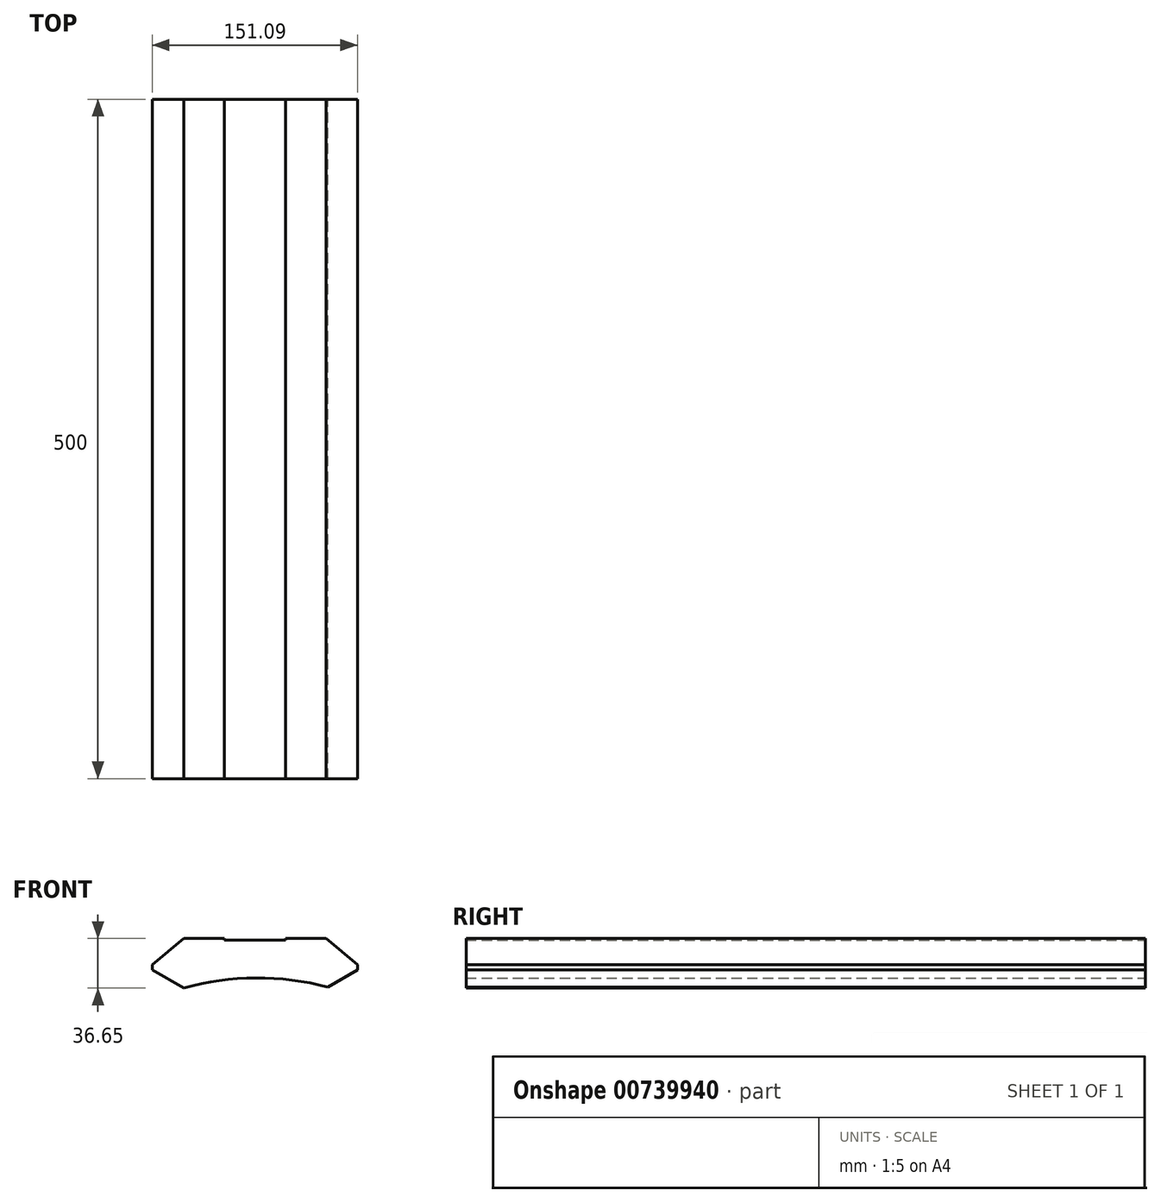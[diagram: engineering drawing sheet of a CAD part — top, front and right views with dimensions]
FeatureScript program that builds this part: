
annotation { "Feature Type Name" : "Feature", "Feature Type Description" : "" }
export const myFeature = defineFeature(function(context is Context, id is Id, definition is map)
    precondition{}
    {
        {
            var Q0;
            Q0=qCreatedBy(makeId("Front.planeOp"),FACE);
            var sketch = newSketch(context, id + "F0", { "sketchPlane" : qUnion([Q0])});
            skLineSegment(sketch, "E0", {"start": v(-68.02, 4) * mm, "end": v(-44.97, 23.34) * mm});
            skLineSegment(sketch, "E1", {"start": v(-44.97, 23.34) * mm, "end": v(-14.97, 23.34) * mm});
            skLineSegment(sketch, "E2", {"start": v(-14.97, 23.34) * mm, "end": v(-14.97, 22.04) * mm});
            skLineSegment(sketch, "E3", {"start": v(-14.97, 22.04) * mm, "end": v(30.03, 22.04) * mm});
            skLineSegment(sketch, "E4", {"start": v(30.03, 22.04) * mm, "end": v(30.03, 23.34) * mm});
            skLineSegment(sketch, "E5", {"start": v(30.03, 23.34) * mm, "end": v(60.03, 23.34) * mm});
            skLineSegment(sketch, "E6", {"start": v(60.03, 23.34) * mm, "end": v(83.07, 4) * mm});
            skLineSegment(sketch, "E7", {"start": v(83.07, 4) * mm, "end": v(83.07, 0) * mm});
            skLineSegment(sketch, "E8", {"start": v(83.07, 0) * mm, "end": v(61.27, -12.6) * mm});
            skLineSegment(sketch, "E9", {"start": v(-68.02, 4) * mm, "end": v(-68.02, 0) * mm});
            skLineSegment(sketch, "E10", {"start": v(-68.02, 0) * mm, "end": v(-44.97, -13.3) * mm});
            skArc(sketch, "E11", {"start": v(61.27, -12.6) * mm, "mid": v(8.1, -5.77) * mm, "end": v(-44.97, -13.3) * mm});
            skSolve(sketch);
        }
        {
            var Q0;
            Q0=makeQuery(id+"F0.imprint","IMPRINT",FACE,{"disambiguationData":[TD([[makeQuery(id+"F0.imprint","IMPRINT",EDGE,{"derivedFrom":sQuery(id+"F0.wireOp",EDGE,"E0")}),-1.0]])]});
            extrude(context, id + "F1", {"entities" : qUnion([Q0]), "endBound" : BoundingType.SYMMETRIC, "depth" : 500 * mm, "offsetDistance" : 25 * mm});
        }
    });
